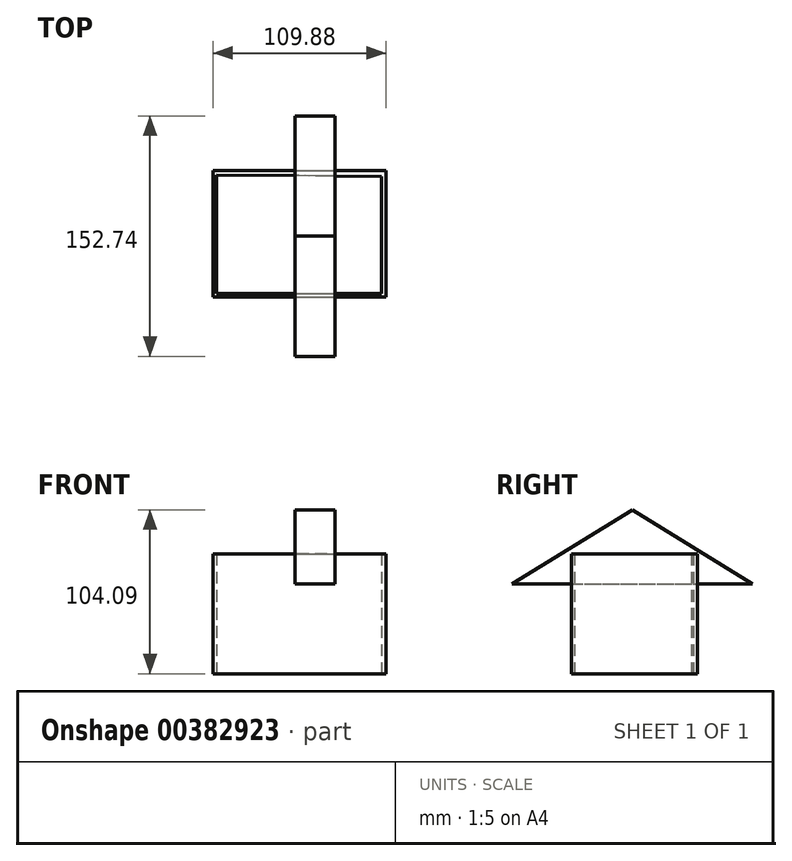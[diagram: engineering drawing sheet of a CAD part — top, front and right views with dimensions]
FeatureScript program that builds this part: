
annotation { "Feature Type Name" : "Feature", "Feature Type Description" : "" }
export const myFeature = defineFeature(function(context is Context, id is Id, definition is map)
    precondition{}
    {
        {
            var Q0;
            Q0=qCreatedBy(makeId("Top.planeOp"),FACE);
            var sketch = newSketch(context, id + "F0", { "sketchPlane" : qUnion([Q0])});
            skLineSegment(sketch, "E0.bottom", {"start": v(-52.17, 41.54) * mm, "end": v(57.71, 41.54) * mm});
            skLineSegment(sketch, "E0.top", {"start": v(-52.17, -38.62) * mm, "end": v(57.71, -38.62) * mm});
            skLineSegment(sketch, "E0.left", {"start": v(-52.17, 41.54) * mm, "end": v(-52.17, -38.62) * mm});
            skLineSegment(sketch, "E0.right", {"start": v(57.71, 41.54) * mm, "end": v(57.71, -38.62) * mm});
            skSolve(sketch);
        }
        {
            var Q0;
            Q0=makeQuery(id+"F0.imprint","IMPRINT",FACE,{"disambiguationData":[TD([[makeQuery(id+"F0.imprint","IMPRINT",EDGE,{"derivedFrom":sQuery(id+"F0.wireOp",EDGE,"E0.bottom")}),-1.0]])]});
            var sketch = newSketch(context, id + "F1", { "sketchPlane" : qUnion([Q0])});
            skLineSegment(sketch, "E1", {"start": v(-49.84, 38.91) * mm, "end": v(-49.84, -36.58) * mm});
            skLineSegment(sketch, "E2", {"start": v(-49.84, -36.58) * mm, "end": v(54.8, -36.58) * mm});
            skLineSegment(sketch, "E3", {"start": v(54.8, -36.58) * mm, "end": v(54.8, 37.75) * mm});
            skLineSegment(sketch, "E4", {"start": v(54.8, 37.75) * mm, "end": v(-49.84, 38.91) * mm});
            skSolve(sketch);
        }
        {
            var Q0;
            Q0 = qSketchRegion(id + "F1", true);
            var Q1;
            Q1=makeQuery(id+"F0.imprint","IMPRINT",FACE,{"disambiguationData":[TD([[makeQuery(id+"F0.imprint","IMPRINT",EDGE,{"derivedFrom":sQuery(id+"F0.wireOp",EDGE,"E0.bottom")}),-1.0]])]});
            extrude(context, id + "F2", {"entities" : qUnion([Q0, Q1]), "depth" : 76.2 * mm});
        }
        {
            var Q0;
            Q0=qCreatedBy(makeId("Right.planeOp"),FACE);
            var sketch = newSketch(context, id + "F3", { "sketchPlane" : qUnion([Q0])});
            skLineSegment(sketch, "E5", {"start": v(-76.37, 56.87) * mm, "end": v(76.37, 56.87) * mm});
            skLineSegment(sketch, "E6", {"start": v(76.37, 56.87) * mm, "end": v(0, 104.1) * mm});
            skLineSegment(sketch, "E7", {"start": v(0, 104.1) * mm, "end": v(-76.37, 56.87) * mm});
            skSolve(sketch);
        }
        {
            var Q0;
            Q0=makeQuery(id+"F3.imprint","IMPRINT",FACE,{"disambiguationData":[TD([[makeQuery(id+"F3.imprint","IMPRINT",EDGE,{"derivedFrom":sQuery(id+"F3.wireOp",EDGE,"E5")}),1.0]])]});
            extrude(context, id + "F4", {"entities" : qUnion([Q0]), "depth" : 25.4 * mm});
        }
    });
